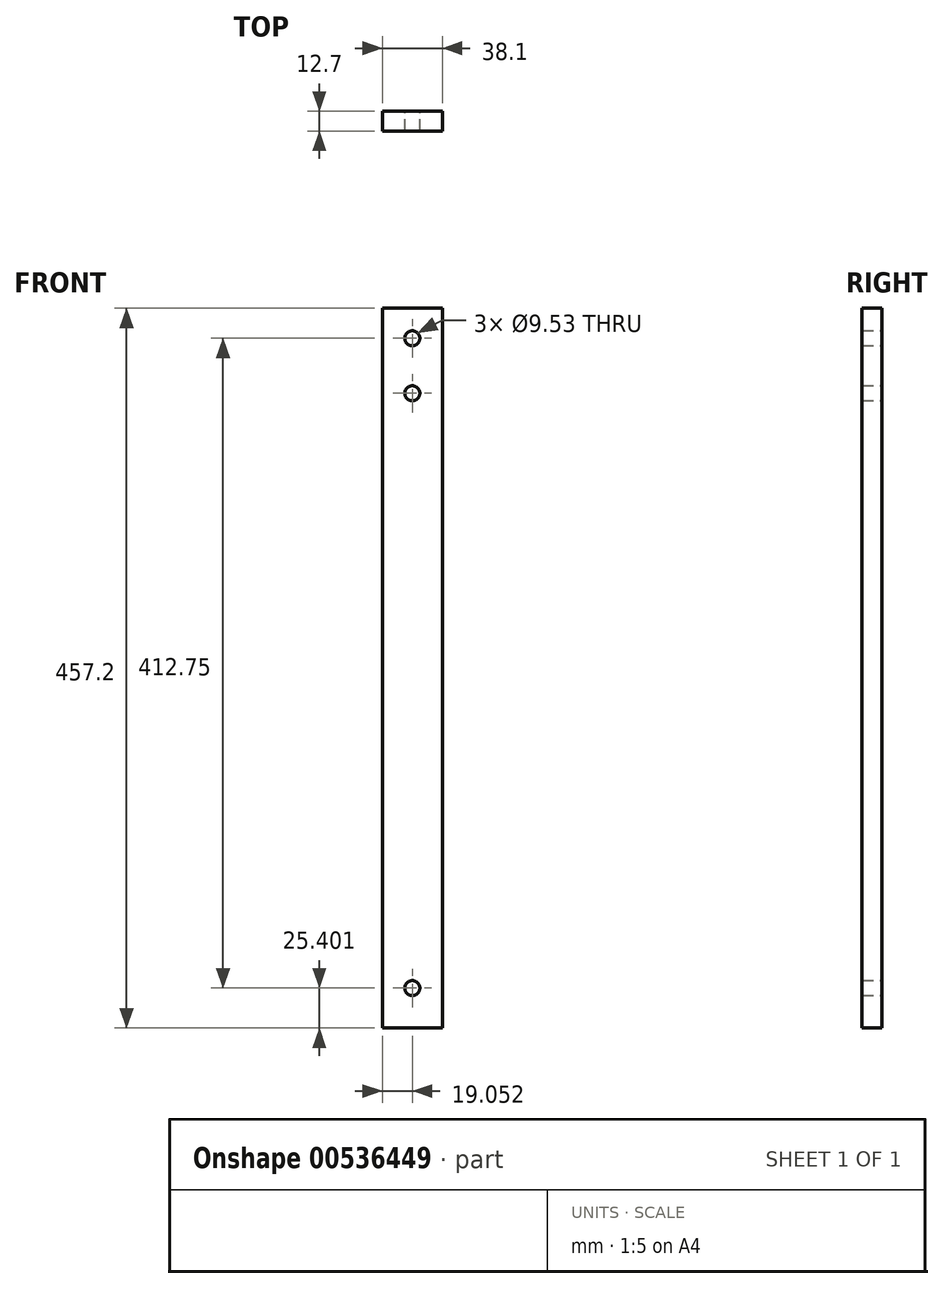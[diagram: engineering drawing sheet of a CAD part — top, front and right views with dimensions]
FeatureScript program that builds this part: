
annotation { "Feature Type Name" : "Feature", "Feature Type Description" : "" }
export const myFeature = defineFeature(function(context is Context, id is Id, definition is map)
    precondition{}
    {
        {
            var Q0;
            Q0=qCreatedBy(makeId("Front.planeOp"),FACE);
            var sketch = newSketch(context, id + "F0", { "sketchPlane" : qUnion([Q0])});
            skLineSegment(sketch, "E0.bottom", {"start": v(-23.72, 429.74) * mm, "end": v(14.38, 429.74) * mm});
            skLineSegment(sketch, "E0.top", {"start": v(-23.72, -27.46) * mm, "end": v(14.38, -27.46) * mm});
            skLineSegment(sketch, "E0.left", {"start": v(-23.72, 429.74) * mm, "end": v(-23.72, -27.46) * mm});
            skLineSegment(sketch, "E0.right", {"start": v(14.38, 429.74) * mm, "end": v(14.38, -27.46) * mm});
            skCircle(sketch, "E1", {"center": v(-4.67, -2.06) * mm, "radius": 4.76 * mm});
            skCircle(sketch, "E2", {"center": v(-4.67, 410.7) * mm, "radius": 4.76 * mm});
            skCircle(sketch, "E3", {"center": v(-4.67, 375.77) * mm, "radius": 4.76 * mm});
            skLineSegment(sketch, "E4", {"start": v(-4.67, 410.7) * mm, "end": v(-4.67, 429.74) * mm});
            skLineSegment(sketch, "E5", {"start": v(-4.67, 410.7) * mm, "end": v(-4.67, 375.77) * mm});
            skLineSegment(sketch, "E6", {"start": v(-4.67, -2.06) * mm, "end": v(-4.67, -27.46) * mm});
            skSolve(sketch);
        }
        {
            var Q0;
            Q0 = qSketchRegion(id + "F0", true);
            extrude(context, id + "F1", {"entities" : qUnion([Q0]), "depth" : 12.7 * mm, "offsetDistance" : 25.4 * mm});
        }
    });
